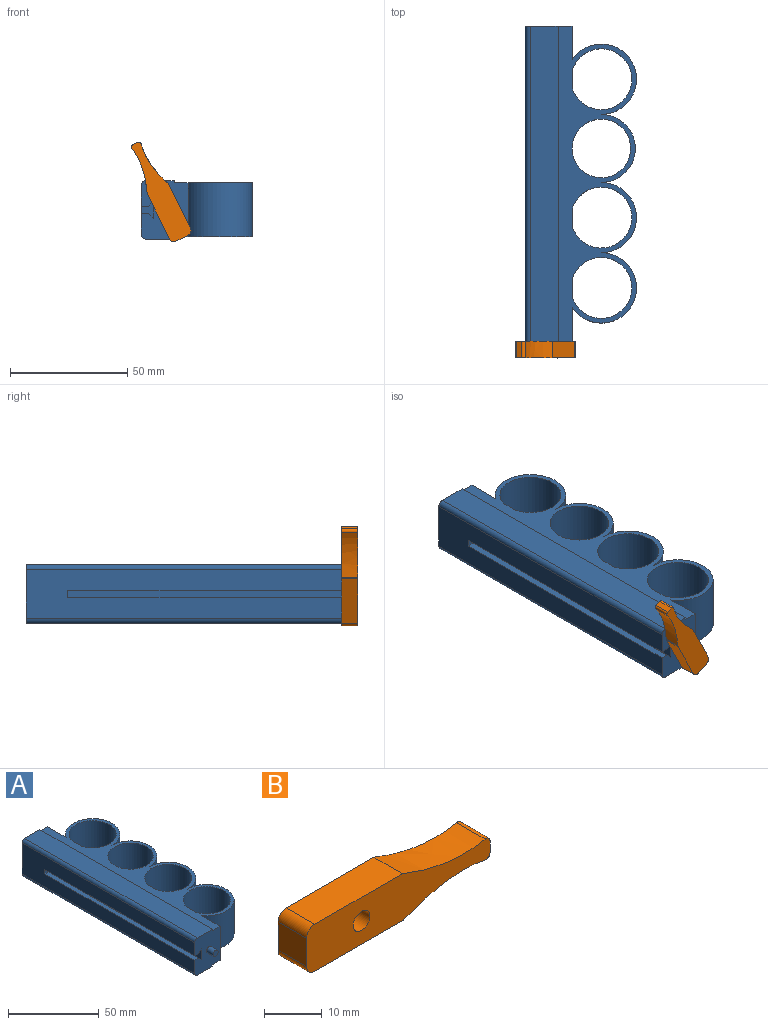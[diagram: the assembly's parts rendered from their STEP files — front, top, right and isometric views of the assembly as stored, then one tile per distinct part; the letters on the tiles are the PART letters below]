
ASSEMBLY  parts=2 mates=1
PART A: 32 faces, bbox 47.5x139.6x25 mm
  f0: plane 134.58x33.46mm, normal (0,0,1), area 1553.9mm2, adj f1,f2,f3,f4,f5,f6,f7,f8
  f1: plane 25x19.96mm, normal (0,1,0), area 485.2mm2, adj f0,f9,f15,f25,f26,f27,f28,f29
  f2: plane 23x7.14mm, normal (1,0,0), area 164.3mm2, adj f0,f11,f27
  f3: plane 23x7.14mm, normal (1,0,0), area 164.3mm2, adj f0,f13,f27
  f4: plane 23x7.14mm, normal (1,0,0), area 164.3mm2, adj f0,f14,f27
  f5: cylinder r=15mm len=30mm, axis (0,0,-1), area 1423.7mm2, adj f0,f6,f10,f27
  f6: cylinder r=15mm len=30mm, axis (0,0,-1), area 1083.8mm2, adj f0,f5,f7,f27
  f7: cylinder r=14.5mm len=29mm, axis (0,0,-1), area 1047.7mm2, adj f0,f6,f8,f27
  f8: cylinder r=15mm len=30mm, axis (0,0,-1), area 1423.7mm2, adj f0,f7,f9,f27
  f9: plane 23x14.43mm, normal (1,0,0), area 331.8mm2, adj f0,f1,f8,f27
  f10: plane 23x14.57mm, normal (1,0,0), area 335.1mm2, adj f0,f5,f16,f27
  f11: cylinder r=13mm len=26mm, axis (0,0,-1), area 1712.3mm2, adj f0,f2,f27
  f12: cylinder r=12.5mm len=25mm, axis (0,0,-1), area 1806.4mm2, adj f0,f27
  f13: cylinder r=13mm len=26mm, axis (0,0,-1), area 1712.3mm2, adj f0,f3,f27
  f14: cylinder r=13mm len=26mm, axis (0,0,-1), area 1712.3mm2, adj f0,f4,f27
  f15: plane 134.58x20.8mm, normal (-1,0,0), area 2448.8mm2, adj f1,f16,f17,f18,f22,f25,f26
  f16: plane 25x19.96mm, normal (0,-1,0), area 452.7mm2, adj f0,f10,f15,f17,f18,f19,f20,f21
  f17: plane 116.8x3mm, normal (0,0,-1), area 350.4mm2, adj f15,f16,f21,f22
  f18: plane 116.8x3mm, normal (0,0,1), area 350.4mm2, adj f15,f16,f19,f22
  f19: plane 116.8x2.12mm, normal (0.71,0,0.71), area 350.4mm2, adj f16,f18,f20,f22
  f20: plane 116.8x7.24mm, normal (-1,0,0), area 845.9mm2, adj f16,f19,f21,f22
  f21: plane 116.8x2.12mm, normal (0.71,0,-0.71), area 350.4mm2, adj f16,f17,f20,f22
  f22: plane 7.24x5.12mm, normal (0,-1,0), area 19.9mm2, adj f15,f17,f18,f19,f20,f21
  f23: cylinder r=2mm len=5mm, axis (0,1,0), area 62.8mm2, adj f16,f24
  f24: plane 4x4mm, normal (0,-1,0), area 12.6mm2, adj f23
  f25: cylinder r=2.1mm len=134.58mm, axis (0,-1,0), area 443.9mm2, adj f1,f15,f16,f28
  f26: cylinder r=2.1mm len=134.58mm, axis (0,1,0), area 443.9mm2, adj f1,f15,f16,f30
  f27: plane 134.58x33.46mm, normal (0,0,-1), area 1553.9mm2, adj f1,f2,f3,f4,f5,f6,f7,f8
  f28: plane 134.58x11.9mm, normal (0,0,-1), area 1601.5mm2, adj f1,f16,f25,f29
  f29: plane 134.58x1mm, normal (1,0,0), area 134.6mm2, adj f1,f16,f27,f28
  f30: plane 134.58x11.9mm, normal (0,0,1), area 1601.5mm2, adj f1,f16,f26,f31
  f31: plane 134.58x1mm, normal (1,0,0), area 134.6mm2, adj f0,f1,f16,f30
PART B: 15 faces, bbox 45x7x10 mm
  f0: plane 45x10mm, normal (0,1,0), area 342.5mm2, adj f2,f3,f4,f7,f8,f9,f10,f11
  f1: plane 45x10mm, normal (0,-1,0), area 329.3mm2, adj f2,f3,f4,f5,f7,f8,f9,f10
  f2: plane 7x2.46mm, normal (1,0,0), area 17.2mm2, adj f0,f1,f13,f14
  f3: plane 21.5x7mm, normal (0,0,1), area 150.5mm2, adj f0,f1,f7,f10
  f4: plane 21.11x7mm, normal (0,0,-1), area 147.8mm2, adj f0,f1,f11,f12
  f5: cylinder r=2.05mm len=5mm, axis (0,-1,0), area 64.4mm2, adj f1,f6
  f6: plane 4.1x4.1mm, normal (0,-1,0), area 13.2mm2, adj f5
  f7: extruded ~20.29x7mm, area 145.5mm2, adj f0,f1,f3,f14
  f8: extruded ~19.94x7mm, area 142.9mm2, adj f0,f1,f12,f13
  f9: plane 7x6mm, normal (-1,0,0), area 42mm2, adj f0,f1,f10,f11
  f10: cylinder r=2mm len=7mm, axis (0,1,0), area 22mm2, adj f0,f1,f3,f9
  f11: cylinder r=2mm len=7mm, axis (0,-1,0), area 22mm2, adj f0,f1,f4,f9
  f12: cylinder r=2mm len=7mm, axis (0,1,0), area 5.3mm2, adj f0,f1,f4,f8
  f13: cylinder r=1mm len=7mm, axis (0,1,0), area 12.5mm2, adj f0,f1,f2,f8
  f14: cylinder r=1mm len=7mm, axis (0,1,0), area 12.5mm2, adj f0,f1,f2,f7
PLACE A t=(-79.9,-30.62,21.8)mm fixed
PLACE B rot(axis=(-0.53,0,-0.85),180deg) t=(-26.15,-97.98,76.46)mm
MATE revolute B.f5 <-> A.f23  axis (0,1,0) through (-111.4,-102.98,34.3)mm
